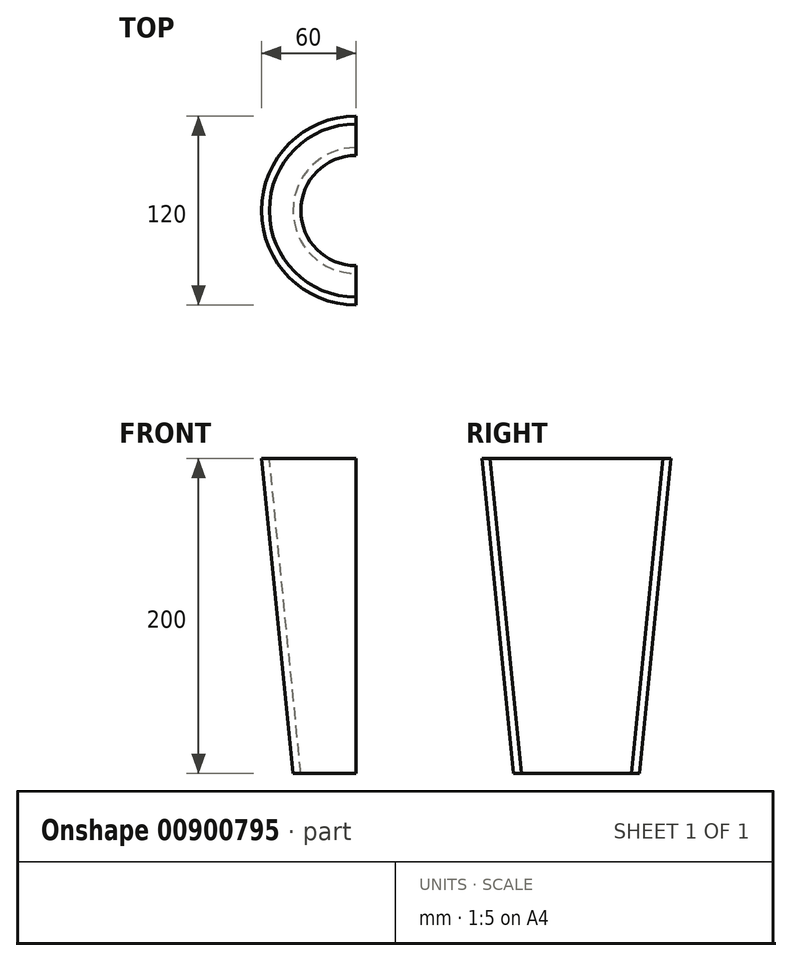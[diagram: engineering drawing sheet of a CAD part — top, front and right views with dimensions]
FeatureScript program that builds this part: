
annotation { "Feature Type Name" : "Feature", "Feature Type Description" : "" }
export const myFeature = defineFeature(function(context is Context, id is Id, definition is map)
    precondition{}
    {
        {
            var Q0;
            Q0=qCreatedBy(makeId("Top.planeOp"),FACE);
            var sketch = newSketch(context, id + "F0", { "sketchPlane" : qUnion([Q0])});
            skArc(sketch, "E0", {"start": v(0, 40) * mm, "mid": v(-40, 0) * mm, "end": v(0, -40) * mm});
            skArc(sketch, "E1", {"start": v(0, 35) * mm, "mid": v(-35, 0) * mm, "end": v(0, -35) * mm});
            skLineSegment(sketch, "E2", {"start": v(0, -40) * mm, "end": v(0, -35) * mm});
            skLineSegment(sketch, "E3.trimOffspring", {"start": v(0, 35) * mm, "end": v(0, 40) * mm});
            skSolve(sketch);
        }
        {
            var Q0;
            Q0=qCreatedBy(makeId("Top.planeOp"),FACE);
            cPlane(context, id + "F1", {"entities" : qUnion([Q0]), "cplaneType" : CPlaneType.OFFSET, "offset" : 200 * mm, "width" : 150 * mm, "height" : 150 * mm});
        }
        {
            var Q0;
            Q0=qCreatedBy(id+"F1.planeOp",FACE);
            var sketch = newSketch(context, id + "F2", { "sketchPlane" : qUnion([Q0])});
            skArc(sketch, "E4", {"start": v(0, 60) * mm, "mid": v(-60, 0) * mm, "end": v(0, -60) * mm});
            skArc(sketch, "E5", {"start": v(0, 55) * mm, "mid": v(-55, 0) * mm, "end": v(0, -55) * mm});
            skLineSegment(sketch, "E6", {"start": v(0, -60) * mm, "end": v(0, -55) * mm});
            skLineSegment(sketch, "E7.trimOffspring", {"start": v(0, 55) * mm, "end": v(0, 60) * mm});
            skSolve(sketch);
        }
        {
            var Q0;
            Q0=makeQuery(id+"F2.imprint","IMPRINT",FACE,{"disambiguationData":[TD([[makeQuery(id+"F2.imprint","IMPRINT",EDGE,{"derivedFrom":sQuery(id+"F2.wireOp",EDGE,"E4")}),1.0]])]});
            var Q1;
            Q1=makeQuery(id+"F0.imprint","IMPRINT",FACE,{"disambiguationData":[TD([[makeQuery(id+"F0.imprint","IMPRINT",EDGE,{"derivedFrom":sQuery(id+"F0.wireOp",EDGE,"E0")}),1.0]])]});
            loft(context, id + "F3", {"sheetProfilesArray" : [{ "sheetProfileEntities" : qUnion([Q0]) }, { "sheetProfileEntities" : qUnion([Q1]) }]});
        }
    });
